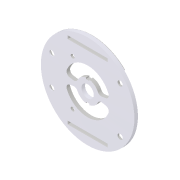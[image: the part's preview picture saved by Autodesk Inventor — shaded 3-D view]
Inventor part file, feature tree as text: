
AUTODESK INVENTOR PART (.ipt)
format: ipt  version: 2018 (Build 220112000, 112)  size: 361,984 bytes
history: native  units: in
note: dims shown in document units (in); Inventor stores cm internally (conversion verified against a paired STEP export)
features: extrude x12, sketch x12, fillet x3, mirror x1, chamfer x1
ambient origin geometry x8: Origin, YZ Plane, XZ Plane, XY Plane, X Axis, Y Axis, Z Axis, Center Point
bodies: Solid1 (feature_tree)
feature tree (29):
  extrude  "Extrusion1"  Depth=0.1181in TaperAngle=0.0deg
  extrude  "Extrusion2"  Depth=0.1181in TaperAngle=0.0deg
  extrude  "Extrusion3"  Depth=0.689in
  extrude  "Extrusion4"  Depth=0.1732in
  fillet  "Fillet1"  Radius=0.5in
  fillet  "Fillet2"  Radius=1.2in
  extrude  "Extrusion5"  Depth=0.75in
  mirror  "Mirror1"
  chamfer  "Chamfer1"  Distance=1.0in
  extrude  "Extrusion6"  Depth=0.125in
  extrude  "Extrusion7"  Depth=1.3in
  extrude  "Extrusion8"  Depth=1.2in
  extrude  "Extrusion9"  Depth=0.0197in TaperAngle=45.0deg
  extrude  "Extrusion10"  Depth=0.5in
  extrude  "Extrusion11"  Depth=0.0256in TaperAngle=0.0deg
  extrude  "Extrusion13"  Depth=0.0256in TaperAngle=0.0deg
  fillet  "Fillet3"  Radius=0.75in
  sketch  "Sketch1"  dims[d0=3.125in d1=0.1181in d2=0.0in]
  sketch  "Sketch2"  dims[d3=0.4125in d4=0.1181in d5=0.0in]
  sketch  "Sketch3"  dims[d6=0.1181in d7=0.689in]
  sketch  "Sketch4"  dims[d8=0.1181in d9=0.0in d10=0.1732in d11=0.5in d12=1.2in]
  sketch  "Sketch6"  dims[d13=1.5in d14=0.75in]
  sketch  "Sketch7"  dims[d15=0.0687in d16=1.0in d17=0.0in]
  sketch  "Sketch8"  dims[d18=0.125in d19=0.125in]
  sketch  "Sketch9"  dims[d20=0.07in d21=1.3in]
  sketch  "Sketch11"  dims[d22=0.65in d23=1.2in]
  sketch  "Sketch12"  dims[d24=0.0984in d25=0.0in d26=0.0197in d27=0.125in d28=45.0deg]
  sketch  "Sketch13"  dims[d29=0.1299in d30=0.5in]
  sketch  "Sketch17"  dims[d31=0.7638in d32=1.0359in d33=0.0in d35=0.0866in d36=0.0in d37=0.75in d38=0.375in d39=0.2953in d40=0.2362in d41=0.2362in d42=0.0866in d43=0.0in d44=0.2362in d45=0.1732in d46=1.0in d47=0.0in d48=2.9003in d50=0.0472in d51=0.1181in d52=0.0591in d53=1.0in d54=0.0in d57=0.2953in d58=0.2953in d59=0.0866in d60=0.0in d67=1.0866in d69=0.1732in d70=0.2362in d72=0.7874in d84=3.125in d85=3.025in d86=45.0deg d87=45.0deg d88=0.0394in d89=0.0in d90=0.0256in d91=1.0866in d92=0.7705in]
